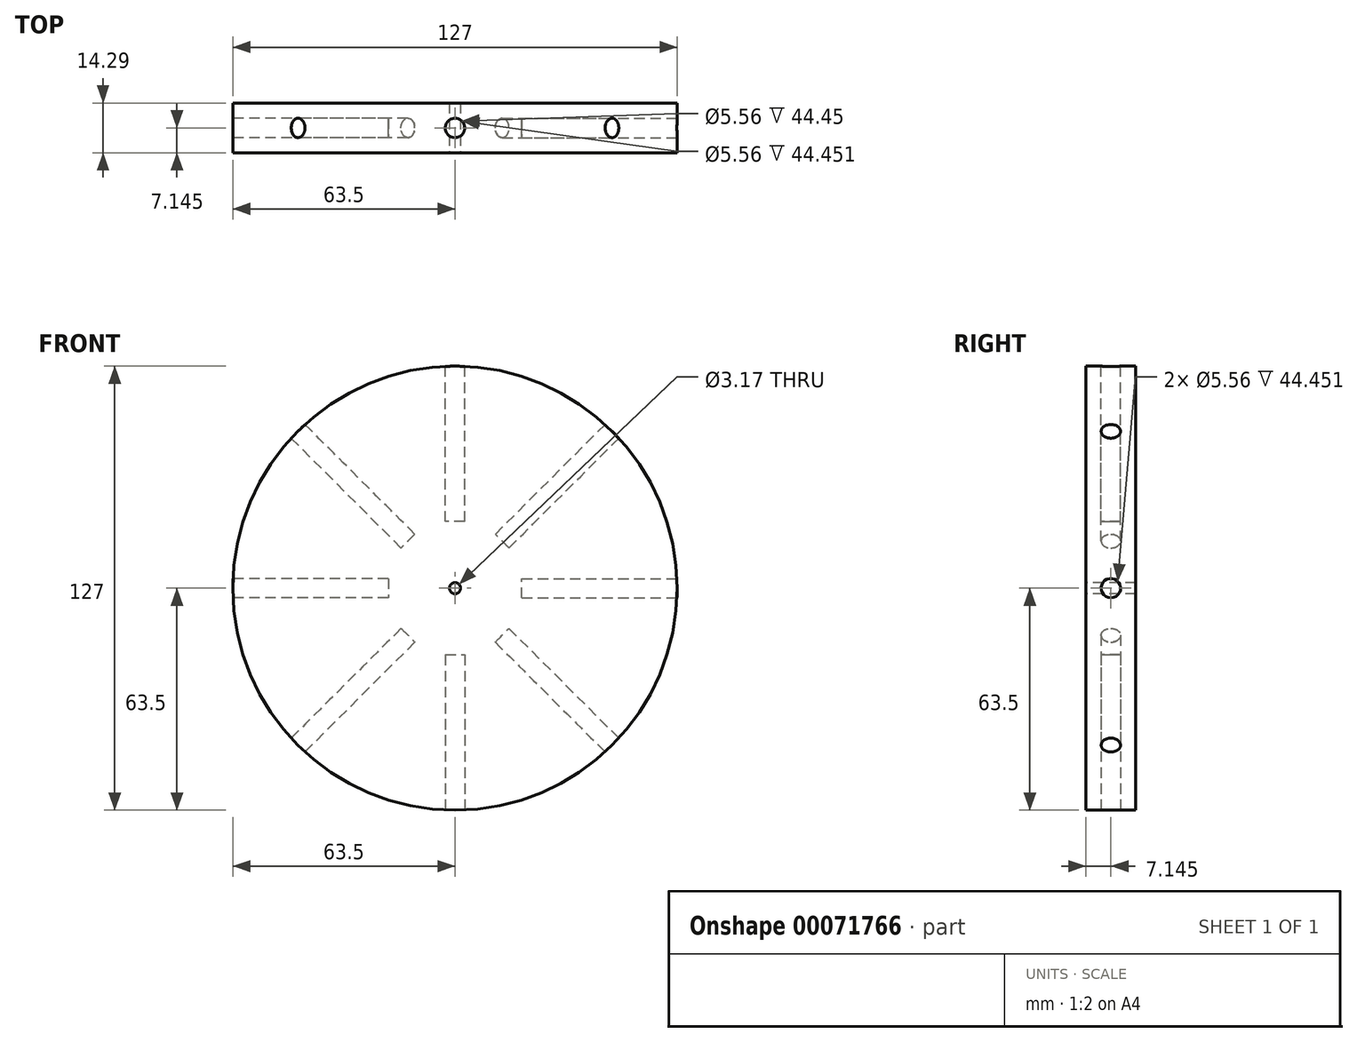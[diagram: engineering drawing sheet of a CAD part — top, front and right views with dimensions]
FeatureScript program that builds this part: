
annotation { "Feature Type Name" : "Feature", "Feature Type Description" : "" }
export const myFeature = defineFeature(function(context is Context, id is Id, definition is map)
    precondition{}
    {
        {
            var Q0;
            Q0=qCreatedBy(makeId("Front.planeOp"),FACE);
            var sketch = newSketch(context, id + "F0", { "sketchPlane" : qUnion([Q0])});
            skCircle(sketch, "E0", {"center": v(0, 0) * mm, "radius": 63.5 * mm});
            skSolve(sketch);
        }
        {
            var Q0;
            Q0=makeQuery(id+"F0.imprint","IMPRINT",FACE,{"disambiguationData":[TD([[makeQuery(id+"F0.imprint","IMPRINT",EDGE,{"derivedFrom":sQuery(id+"F0.wireOp",EDGE,"E0")}),1.0]])]});
            extrude(context, id + "F1", {"entities" : qUnion([Q0]), "depth" : 6.35 * mm});
        }
        {
            var Q0;
            Q0=makeQuery(id+"F1.opExtrude","CAP_FACE",FACE,{"disambiguationData":[OSD([sQuery(id+"F0.wireOp",EDGE,"E0")])],"isStart":false});
            var sketch = newSketch(context, id + "F2", { "sketchPlane" : qUnion([Q0])});
            skCircle(sketch, "E1.0", {"center": v(0, 0) * mm, "radius": 63.5 * mm});
            skCircle(sketch, "E2", {"center": v(0, 0) * mm, "radius": 1.59 * mm});
            skSolve(sketch);
        }
        {
            var Q0;
            Q0=makeQuery(id+"F2.imprint","IMPRINT",FACE,{"disambiguationData":[TD([[makeQuery(id+"F2.imprint","IMPRINT",EDGE,{"derivedFrom":sQuery(id+"F2.wireOp",EDGE,"E2")}),1.0]])]});
            extrude(context, id + "F3", {"entities" : qUnion([Q0]), "operationType" : NewBodyOperationType.REMOVE, "endBound" : BoundingType.THROUGH_ALL, "oppositeDirection" : true, "depth" : 25.4 * mm});
        }
        {
            var Q0;
            Q0=makeQuery(id+"F1.opExtrude","CAP_FACE",FACE,{"disambiguationData":[OSD([sQuery(id+"F0.wireOp",EDGE,"E0")])],"isStart":true});
            var sketch = newSketch(context, id + "F4", { "sketchPlane" : qUnion([Q0])});
            skLineSegment(sketch, "E3", {"start": v(0, 0) * mm, "end": v(-63.5, 0) * mm, "construction": true});
            skSolve(sketch);
        }
        {
            var Q0;
            Q0=sQuery(id+"F4.wireOp",VERTEX,"E3.end");
            var Q1;
            Q1=sQuery(id+"F4.wireOp",EDGE,"E3");
            cPlane(context, id + "F5", {"entities" : qUnion([Q0, Q1]), "cplaneType" : CPlaneType.LINE_POINT, "offset" : 152.4 * mm, "width" : 152.4 * mm, "height" : 152.4 * mm});
        }
        {
            var Q0;
            Q0=qCreatedBy(id+"F5.planeOp",FACE);
            var sketch = newSketch(context, id + "F6", { "sketchPlane" : qUnion([Q0])});
            skLineSegment(sketch, "E4.0", {"start": v(-6.35, -63.5) * mm, "end": v(-6.35, 63.5) * mm, "construction": true});
            skLineSegment(sketch, "E5", {"start": v(-25.4, 63.5) * mm, "end": v(0, 63.5) * mm, "construction": true});
            skLineSegment(sketch, "E6", {"start": v(0, -63.5) * mm, "end": v(-25.4, -63.5) * mm, "construction": true});
            skLineSegment(sketch, "E7.0", {"start": v(0, -63.5) * mm, "end": v(0, 63.5) * mm, "construction": true});
            skLineSegment(sketch, "E8", {"start": v(0, 63.5) * mm, "end": v(0, -63.5) * mm, "construction": true});
            skLineSegment(sketch, "E9", {"start": v(-3.18, -63.5) * mm, "end": v(-3.18, 63.5) * mm, "construction": true});
            skCircle(sketch, "E10", {"center": v(-3.18, 0) * mm, "radius": 2.78 * mm});
            skSolve(sketch);
        }
        {
            var Q0;
            Q0=makeQuery(id+"F6.imprint","IMPRINT",FACE,{"disambiguationData":[TD([[makeQuery(id+"F6.imprint","IMPRINT",EDGE,{"derivedFrom":sQuery(id+"F6.wireOp",EDGE,"E10")}),1.0]])]});
            extrude(context, id + "F7", {"entities" : qUnion([Q0]), "oppositeDirection" : true, "depth" : 44.45 * mm});
        }
        {
            var Q0;
            Q0=makeQuery(id+"F7.opExtrude","SWEPT_BODY",BODY,{"disambiguationData":[OSD([sQuery(id+"F6.wireOp",EDGE,"E10")])]});
            var Q1;
            Q1=makeQuery(id+"F1.opExtrude","CAP_EDGE",EDGE,{"disambiguationData":[OSD([sQuery(id+"F0.wireOp",EDGE,"E0")])],"isStart":false});
            circularPattern(context, id + "F8", {"entities" : qUnion([Q0]), "axis" : qUnion([Q1]), "angle" : 360 * degree, "instanceCount" : 8, "equalSpace" : true});
        }
        {
            var Q0;
            Q0=makeQuery(id+"F8.opPattern","COPY",BODY,{"derivedFrom":makeQuery(id+"F7.opExtrude","SWEPT_BODY",BODY,{"disambiguationData":[OSD([sQuery(id+"F6.wireOp",EDGE,"E10")])]}),"instanceName":"1"});
            var Q1;
            Q1=makeQuery(id+"F7.opExtrude","SWEPT_BODY",BODY,{"disambiguationData":[OSD([sQuery(id+"F6.wireOp",EDGE,"E10")])]});
            var Q2;
            Q2=makeQuery(id+"F8.opPattern","COPY",BODY,{"derivedFrom":makeQuery(id+"F7.opExtrude","SWEPT_BODY",BODY,{"disambiguationData":[OSD([sQuery(id+"F6.wireOp",EDGE,"E10")])]}),"instanceName":"7"});
            var Q3;
            Q3=makeQuery(id+"F8.opPattern","COPY",BODY,{"derivedFrom":makeQuery(id+"F7.opExtrude","SWEPT_BODY",BODY,{"disambiguationData":[OSD([sQuery(id+"F6.wireOp",EDGE,"E10")])]}),"instanceName":"2"});
            var Q4;
            Q4=makeQuery(id+"F8.opPattern","COPY",BODY,{"derivedFrom":makeQuery(id+"F7.opExtrude","SWEPT_BODY",BODY,{"disambiguationData":[OSD([sQuery(id+"F6.wireOp",EDGE,"E10")])]}),"instanceName":"3"});
            var Q5;
            Q5=makeQuery(id+"F8.opPattern","COPY",BODY,{"derivedFrom":makeQuery(id+"F7.opExtrude","SWEPT_BODY",BODY,{"disambiguationData":[OSD([sQuery(id+"F6.wireOp",EDGE,"E10")])]}),"instanceName":"4"});
            var Q6;
            Q6=makeQuery(id+"F8.opPattern","COPY",BODY,{"derivedFrom":makeQuery(id+"F7.opExtrude","SWEPT_BODY",BODY,{"disambiguationData":[OSD([sQuery(id+"F6.wireOp",EDGE,"E10")])]}),"instanceName":"5"});
            var Q7;
            Q7=makeQuery(id+"F8.opPattern","COPY",BODY,{"derivedFrom":makeQuery(id+"F7.opExtrude","SWEPT_BODY",BODY,{"disambiguationData":[OSD([sQuery(id+"F6.wireOp",EDGE,"E10")])]}),"instanceName":"6"});
            var Q8;
            Q8=makeQuery(id+"F1.opExtrude","SWEPT_BODY",BODY,{"disambiguationData":[OSD([sQuery(id+"F0.wireOp",EDGE,"E0")])]});
            booleanBodies(context, id + "F9", {"operationType" : BooleanOperationType.SUBTRACTION, "tools" : qUnion([Q0, Q1, Q2, Q3, Q4, Q5, Q6, Q7]), "targets" : qUnion([Q8])});
        }
        {
            var Q0;
            Q0=makeQuery(id+"F1.opExtrude","CAP_FACE",FACE,{"disambiguationData":[OSD([sQuery(id+"F0.wireOp",EDGE,"E0")])],"isStart":false});
            extrude(context, id + "F10", {"entities" : qUnion([Q0]), "operationType" : NewBodyOperationType.ADD, "depth" : 1.59 * mm});
        }
        {
            var Q0;
            {var subQ0=sQuery(id+"F0.wireOp",EDGE,"E0");Q0=makeQuery(id+"F4.imprint","IMPRINT",FACE,{"disambiguationData":[TD([[makeQuery(id+"F4.imprint","IMPRINT",EDGE,{"derivedFrom":makeQuery(id+"F1.opExtrude","CAP_EDGE",EDGE,{"disambiguationData":[OSD([subQ0])],"isStart":true})}),-1.0]])]});}
            extrude(context, id + "F11", {"entities" : qUnion([Q0]), "operationType" : NewBodyOperationType.ADD, "depth" : 1.59 * mm});
        }
        {
            var Q0;
            Q0=makeQuery(id+"F10.opExtrude","CAP_FACE",FACE,{"disambiguationData":[OSD([sQuery(id+"F0.wireOp",EDGE,"E0")])],"isStart":false});
            extrude(context, id + "F12", {"entities" : qUnion([Q0]), "operationType" : NewBodyOperationType.ADD, "depth" : 2.38 * mm});
        }
        {
            var Q0;
            Q0=makeQuery(id+"F11.opExtrude","CAP_FACE",FACE,{"disambiguationData":[OSD([sQuery(id+"F0.wireOp",EDGE,"E0"),sQuery(id+"F2.wireOp",EDGE,"E2")])],"isStart":false});
            extrude(context, id + "F13", {"entities" : qUnion([Q0]), "operationType" : NewBodyOperationType.ADD, "depth" : 2.38 * mm});
        }
    });
